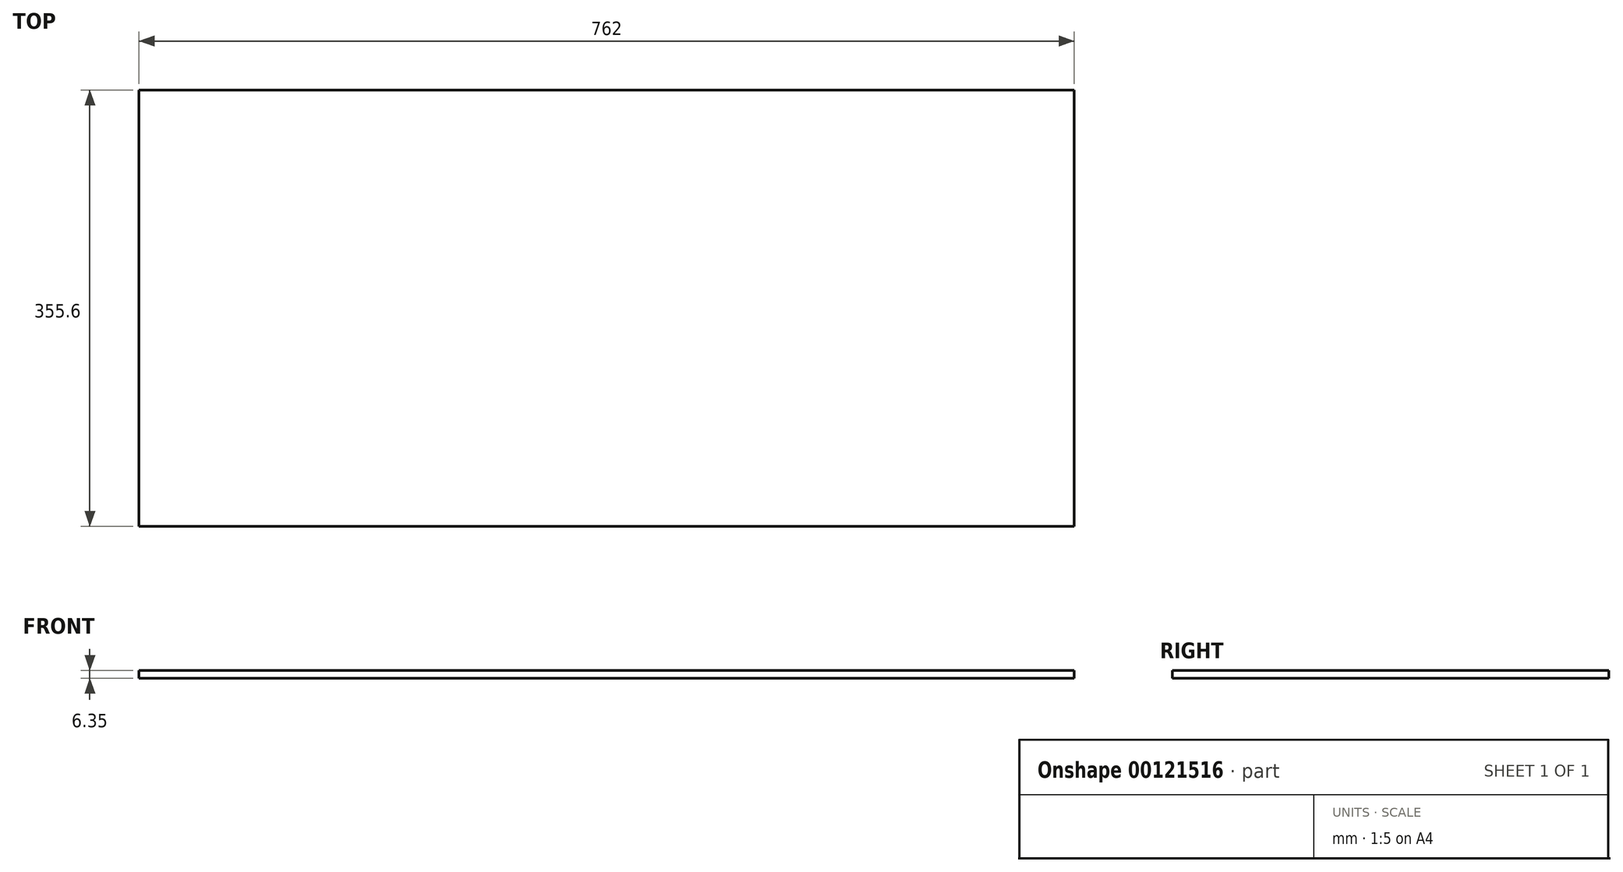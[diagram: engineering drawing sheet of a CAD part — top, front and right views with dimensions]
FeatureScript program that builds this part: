
annotation { "Feature Type Name" : "Feature", "Feature Type Description" : "" }
export const myFeature = defineFeature(function(context is Context, id is Id, definition is map)
    precondition{}
    {
        {
            var Q0;
            Q0=qCreatedBy(makeId("Top.planeOp"),FACE);
            var sketch = newSketch(context, id + "F0", { "sketchPlane" : qUnion([Q0])});
            skLineSegment(sketch, "E0.bottom", {"start": v(381, 177.8) * mm, "end": v(-381, 177.8) * mm});
            skLineSegment(sketch, "E0.top", {"start": v(381, -177.8) * mm, "end": v(-381, -177.8) * mm});
            skLineSegment(sketch, "E0.left", {"start": v(381, 177.8) * mm, "end": v(381, -177.8) * mm});
            skLineSegment(sketch, "E0.right", {"start": v(-381, 177.8) * mm, "end": v(-381, -177.8) * mm});
            skPoint(sketch, "E0.middle", {"position": v(0, 0) * mm});
            skSolve(sketch);
        }
        {
            var Q0;
            Q0 = qSketchRegion(id + "F0", true);
            extrude(context, id + "F1", {"entities" : qUnion([Q0]), "depth" : 6.35 * mm});
        }
    });
